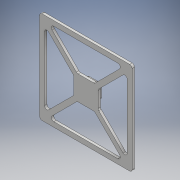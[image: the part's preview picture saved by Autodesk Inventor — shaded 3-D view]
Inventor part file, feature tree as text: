
AUTODESK INVENTOR PART (.ipt)
format: ipt  version: 2018 (Build 220112000, 112)  size: 221,696 bytes
history: native  units: mm
features: extrude x4, sketch x4, fillet x3, projected_geometry x3
ambient origin geometry x8: Origin, YZ Plane, XZ Plane, XY Plane, X Axis, Y Axis, Z Axis, Center Point
bodies: Solid1 (feature_tree)
feature tree (14):
  extrude  "Extrusion1"  Depth=190.0mm
  extrude  "Extrusion2"  Depth=30.0mm
  extrude  "Extrusion3"  Depth=12.0mm TaperAngle=0.0deg
  fillet  "Fillet1"  Radius=20.0mm
  fillet  "Fillet2"  Radius=5.0mm
  extrude  "Extrusion4"  Depth=5.0mm
  fillet  "Fillet3"  Radius=5.0mm
  sketch  "Sketch1"  dims[d0=190.0mm d1=190.0mm]
  sketch  "Sketch2"  dims[d2=5.0mm d3=0.0mm d4=30.0mm]
  sketch  "Sketch3"  dims[d5=30.0mm d6=12.0mm d7=0.0mm d9=20.0mm d10=5.0mm]
  sketch  "Sketch5"  dims[d11=11.0mm d12=0.0mm d13=5.0mm d14=5.0mm d22=40.0mm d24=360.0deg d26=32.75mm d27=0.0mm d28=5.0mm]
  projected_geometry  "Projected Loop2"
  projected_geometry  "Projected Loop3"
  projected_geometry  "Projected Loop4"
